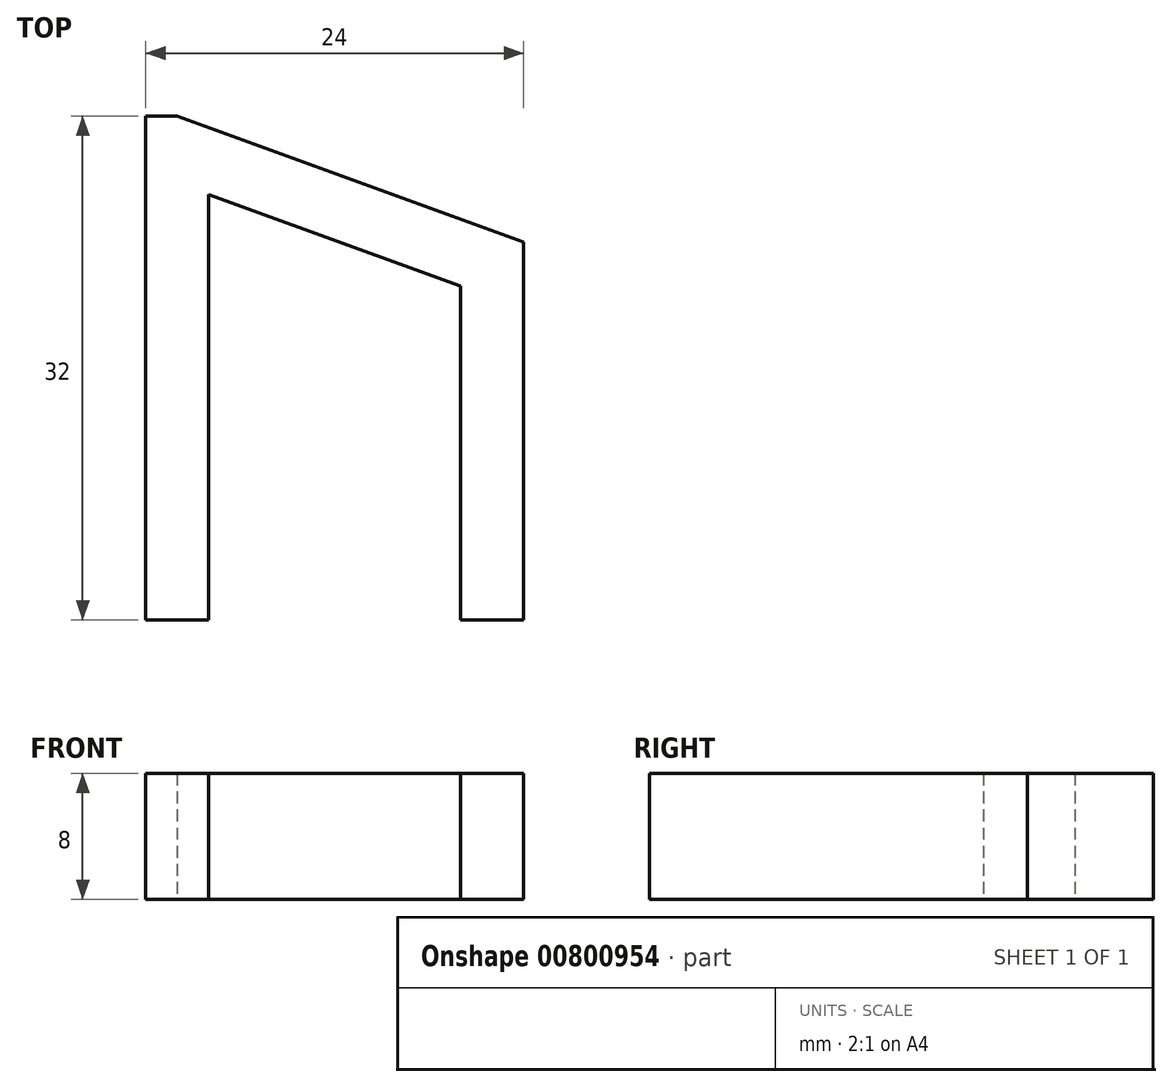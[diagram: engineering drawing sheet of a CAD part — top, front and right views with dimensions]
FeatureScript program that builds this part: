
annotation { "Feature Type Name" : "Feature", "Feature Type Description" : "" }
export const myFeature = defineFeature(function(context is Context, id is Id, definition is map)
    precondition{}
    {
        {
            var Q0;
            Q0=qCreatedBy(makeId("Top.planeOp"),FACE);
            var sketch = newSketch(context, id + "F0", { "sketchPlane" : qUnion([Q0])});
            skLineSegment(sketch, "E0", {"start": v(0, 0) * mm, "end": v(0, -32) * mm});
            skLineSegment(sketch, "E1", {"start": v(0, -32) * mm, "end": v(4, -32) * mm});
            skLineSegment(sketch, "E2", {"start": v(4, -32) * mm, "end": v(4, -4.98) * mm});
            skLineSegment(sketch, "E3", {"start": v(4, -4.98) * mm, "end": v(20, -10.8) * mm});
            skLineSegment(sketch, "E4", {"start": v(20, -10.8) * mm, "end": v(20, -32) * mm});
            skLineSegment(sketch, "E5", {"start": v(20, -32) * mm, "end": v(24, -32) * mm});
            skLineSegment(sketch, "E6", {"start": v(24, -32) * mm, "end": v(24, -8) * mm});
            skLineSegment(sketch, "E7", {"start": v(24, -8) * mm, "end": v(2, 0) * mm});
            skLineSegment(sketch, "E8", {"start": v(2, 0) * mm, "end": v(0, 0) * mm});
            skLineSegment(sketch, "E9", {"start": v(4, -32) * mm, "end": v(20, -32) * mm, "construction": true});
            skSolve(sketch);
        }
        {
            var Q0;
            Q0=makeQuery(id+"F0.imprint","IMPRINT",FACE,{"disambiguationData":[TD([[makeQuery(id+"F0.imprint","IMPRINT",EDGE,{"derivedFrom":sQuery(id+"F0.wireOp",EDGE,"E0")}),1.0]])]});
            extrude(context, id + "F1", {"entities" : qUnion([Q0]), "depth" : 8 * mm, "offsetDistance" : 25 * mm});
        }
    });
